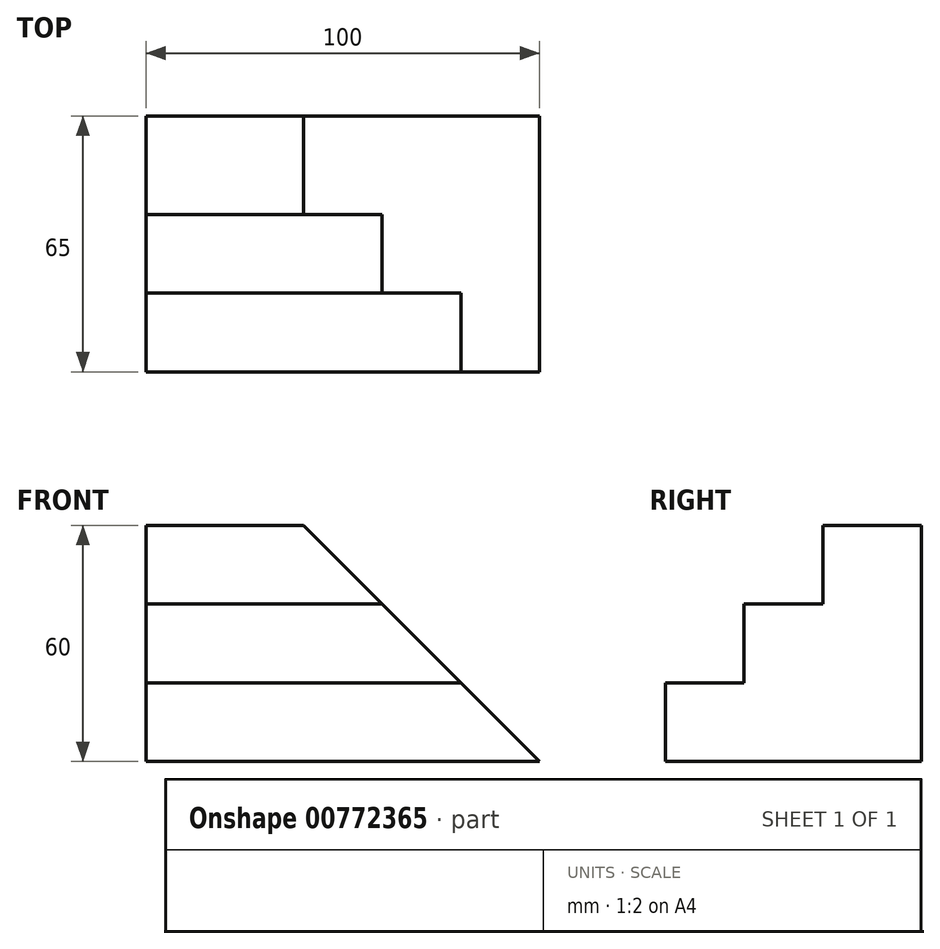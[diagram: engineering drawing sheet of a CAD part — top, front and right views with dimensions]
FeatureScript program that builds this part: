
annotation { "Feature Type Name" : "Feature", "Feature Type Description" : "" }
export const myFeature = defineFeature(function(context is Context, id is Id, definition is map)
    precondition{}
    {
        {
            var Q0;
            Q0=qCreatedBy(makeId("Front.planeOp"),FACE);
            var sketch = newSketch(context, id + "F0", { "sketchPlane" : qUnion([Q0])});
            skLineSegment(sketch, "E0.bottom", {"start": v(0, 0) * mm, "end": v(100, 0) * mm});
            skLineSegment(sketch, "E0.top", {"start": v(0, 60) * mm, "end": v(100, 60) * mm});
            skLineSegment(sketch, "E0.left", {"start": v(0, 0) * mm, "end": v(0, 60) * mm});
            skLineSegment(sketch, "E0.right", {"start": v(100, 0) * mm, "end": v(100, 60) * mm});
            skLineSegment(sketch, "E1", {"start": v(0, 40) * mm, "end": v(100, 40) * mm});
            skLineSegment(sketch, "E2", {"start": v(100, 20) * mm, "end": v(0, 20) * mm});
            skSolve(sketch);
        }
        {
            var Q0;
            Q0 = qSketchRegion(id + "F0", true);
            extrude(context, id + "F1", {"entities" : qUnion([Q0]), "oppositeDirection" : true, "depth" : 25 * mm, "offsetDistance" : 25 * mm});
        }
        {
            var Q0;
            {var subQ0=sQuery(id+"F0.wireOp",EDGE,"E1");Q0=makeQuery(id+"F0.imprint","IMPRINT",FACE,{"disambiguationData":[TD([[makeQuery(id+"F0.imprint","IMPRINT",EDGE,{"derivedFrom":subQ0}),-1.0]])]});}
            var Q1;
            {var subQ0=sQuery(id+"F0.wireOp",EDGE,"E0.bottom");Q1=makeQuery(id+"F0.imprint","IMPRINT",FACE,{"disambiguationData":[TD([[makeQuery(id+"F0.imprint","IMPRINT",EDGE,{"derivedFrom":subQ0}),1.0]])]});}
            extrude(context, id + "F2", {"entities" : qUnion([Q0, Q1]), "operationType" : NewBodyOperationType.ADD, "depth" : 20 * mm, "offsetDistance" : 25 * mm});
        }
        {
            var Q0;
            {var subQ0=sQuery(id+"F0.wireOp",EDGE,"E0.bottom");Q0=makeQuery(id+"F0.imprint","IMPRINT",FACE,{"disambiguationData":[TD([[makeQuery(id+"F0.imprint","IMPRINT",EDGE,{"derivedFrom":subQ0}),1.0]])]});}
            var Q1;
            Q1=makeQuery(id+"F2.opExtrude","CAP_FACE",FACE,{"disambiguationData":[OSD([sQuery(id+"F0.wireOp",EDGE,"E0.bottom"),sQuery(id+"F0.wireOp",EDGE,"E0.left"),sQuery(id+"F0.wireOp",EDGE,"E0.right"),sQuery(id+"F0.wireOp",EDGE,"E1")])],"isStart":false});
            extrude(context, id + "F3", {"entities" : qUnion([Q0]), "operationType" : NewBodyOperationType.ADD, "depth" : 40 * mm, "endBoundEntityFace" : qUnion([Q1]), "offsetDistance" : 25 * mm});
        }
        {
            var Q0;
            Q0=makeQuery(id+"F1.opExtrude","SWEPT_EDGE",EDGE,{"disambiguationData":[OSD([sQuery(id+"F0.wireOp",EDGE,"E0.top"),sQuery(id+"F0.wireOp",EDGE,"E0.right")])]});
            chamfer(context, id + "F4", {"entities" : qUnion([Q0]), "width" : 60 * mm, "tangentPropagation" : true});
        }
    });
